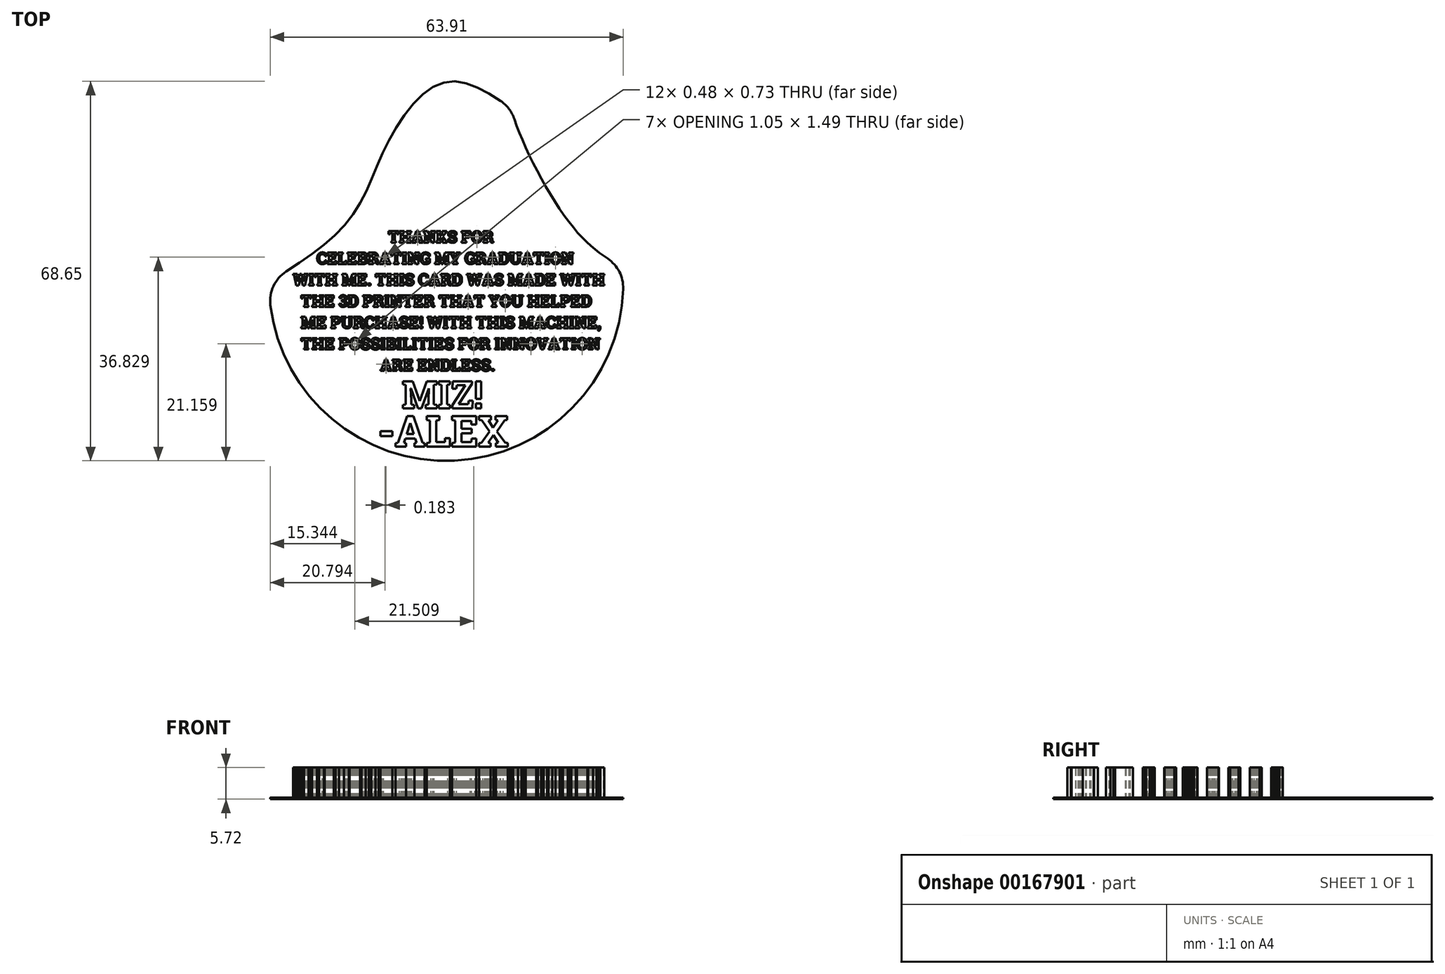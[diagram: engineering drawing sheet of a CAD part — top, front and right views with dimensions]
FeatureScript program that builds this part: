
annotation { "Feature Type Name" : "Feature", "Feature Type Description" : "" }
export const myFeature = defineFeature(function(context is Context, id is Id, definition is map)
    precondition{}
    {
        {
            var Q0;
            Q0=qCreatedBy(makeId("Top.planeOp"),FACE);
            var sketch = newSketch(context, id + "F0", { "sketchPlane" : qUnion([Q0])});
            skText(sketch, "E0", { "text": "                         THANKS FOR \n       CELEBRATING MY GRADUATION \n WITH ME. THIS CARD WAS MADE WITH\n   THE 3D PRINTER THAT YOU HELPED  \n   ME PURCHASE! WITH THIS MACHINE, \n   THE POSSIBILITIES FOR INNOVATION  \n                       ARE ENDLESS.", "fontName": "RobotoSlab-Bold.ttf"});
            skText(sketch, "E1", { "text": "MIZ!", "fontName": "RobotoSlab-Bold.ttf"});
            skText(sketch, "E2", { "text": "-ALEX", "fontName": "RobotoSlab-Bold.ttf"});
            const initialGuessF0  = {"E0": [-0.03303, -0.00568, 1, 0, 0.00211], "E1": [-0.01258, -0.03563, 1, 0, 0.00495], "E2": [-0.01696, -0.04261, 1, 0, 0.0056]};
            skSetInitialGuess(sketch, initialGuessF0);
            skSolve(sketch);
        }
        {
            var Q0;
            Q0 = qSketchRegion(id + "F0", true);
            extrude(context, id + "F1", {"entities" : qUnion([Q0]), "depth" : 5.7 * mm});
        }
        {
            var Q0;
            Q0=qCreatedBy(makeId("Top.planeOp"),FACE);
            var sketch = newSketch(context, id + "F2", { "sketchPlane" : qUnion([Q0])});
            skPoint(sketch, "E3.middle", {"position": v(-49.01, -31.91) * mm});
            skArc(sketch, "E4", {"start": v(-36.38, -17.01) * mm, "mid": v(-3.08, -45.1) * mm, "end": v(27.48, -14.04) * mm});
            skFitSpline(sketch, "E5", {"points": [v(7.22, 18.64) * mm, v(18.5, -3) * mm, v(27.37, -10.29) * mm], "startDerivative": vector(6.75, -28.22) * mm, "endDerivative": vector(20.93, -12.99) * mm});
            skArc(sketch, "E6.trimOffspring", {"start": v(-48.98, -16.59) * mm, "mid": v(-49, -16.59) * mm, "end": v(-49.01, -16.59) * mm});
            skFitSpline(sketch, "E7", {"points": [v(-36.62, -12.87) * mm, v(-21.86, -1.18) * mm, v(-14.86, 12.97) * mm, v(-4.56, 23.39) * mm, v(7.22, 18.64) * mm], "startDerivative": vector(61.53, 38.74) * mm, "endDerivative": vector(53, -36.24) * mm});
            skPoint(sketch, "E8.visualSharp", {"position": v(-37.23, -16.92) * mm});
            skArc(sketch, "E8.filletArc", {"start": v(7.79, 16.66) * mm, "mid": v(6.8, 18.52) * mm, "end": v(5.26, 19.97) * mm});
            skPoint(sketch, "E9.visualSharp", {"position": v(-81.07, -48.43) * mm});
            skArc(sketch, "E9.filletArc", {"start": v(-33.51, -10.9) * mm, "mid": v(-35.83, -13.54) * mm, "end": v(-36.38, -17.01) * mm});
            skPoint(sketch, "E10.visualSharp", {"position": v(-17.08, -45.85) * mm});
            skArc(sketch, "E10.filletArc", {"start": v(27.48, -14.04) * mm, "mid": v(26.77, -10.95) * mm, "end": v(24.66, -8.58) * mm});
            skSolve(sketch);
        }
        {
            var Q0;
            Q0=makeQuery(id+"F2.imprint","IMPRINT",FACE,{"disambiguationData":[TD([[makeQuery(id+"F2.imprint","IMPRINT",EDGE,{"derivedFrom":sQuery(id+"F2.wireOp",EDGE,"E4")}),1.0]])]});
            extrude(context, id + "F3", {"entities" : qUnion([Q0]), "depth" : 0.25 * mm});
        }
    });
